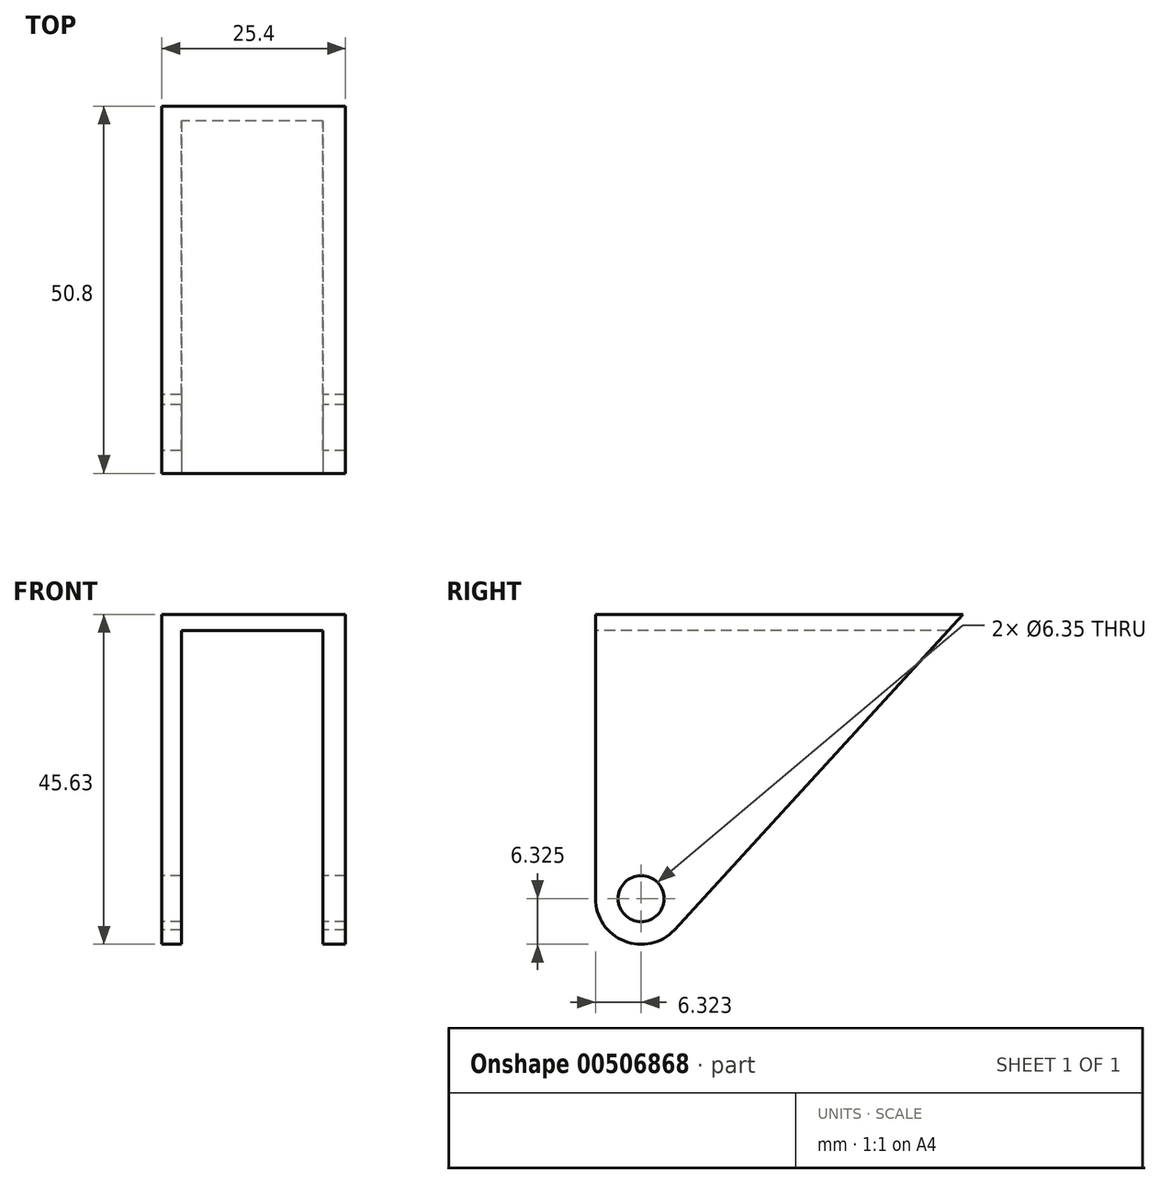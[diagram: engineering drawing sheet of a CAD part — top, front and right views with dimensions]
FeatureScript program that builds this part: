
annotation { "Feature Type Name" : "Feature", "Feature Type Description" : "" }
export const myFeature = defineFeature(function(context is Context, id is Id, definition is map)
    precondition{}
    {
        {
            var Q0;
            Q0=qCreatedBy(makeId("Right.planeOp"),FACE);
            var sketch = newSketch(context, id + "F0", { "sketchPlane" : qUnion([Q0])});
            skLineSegment(sketch, "E0", {"start": v(-6.1, -15.1) * mm, "end": v(-6.1, 24.2) * mm});
            skLineSegment(sketch, "E1", {"start": v(-6.1, 24.2) * mm, "end": v(44.7, 24.2) * mm});
            skLineSegment(sketch, "E2", {"start": v(44.7, 24.2) * mm, "end": v(4.82, -19.43) * mm});
            skArc(sketch, "E3", {"start": v(-6.1, -15.1) * mm, "mid": v(-2.11, -20.97) * mm, "end": v(4.82, -19.43) * mm});
            skSolve(sketch);
        }
        {
            var Q0;
            Q0=makeQuery(id+"FULionVZPmyyQfd_1.opExtrude","SWEPT_FACE",FACE,{"disambiguationData":[OSD([sQuery(id+"F0.wireOp",EDGE,"E2")])]});
            var Q1;
            Q1=makeQuery(id+"FULionVZPmyyQfd_1.opExtrude","SWEPT_FACE",FACE,{"disambiguationData":[OSD([sQuery(id+"F0.wireOp",EDGE,"E1")])]});
            var Q2;
            Q2=makeQuery(id+"F0.imprint","IMPRINT",FACE,{"disambiguationData":[TD([[makeQuery(id+"F0.imprint","IMPRINT",EDGE,{"derivedFrom":sQuery(id+"F0.wireOp",EDGE,"E0")}),-1.0]])]});
            var Q3;
            Q3=makeQuery(id+"FULionVZPmyyQfd_1.opExtrude","CAP_FACE",FACE,{"disambiguationData":[OSD([sQuery(id+"F0.wireOp",EDGE,"E0"),sQuery(id+"F0.wireOp",EDGE,"E1"),sQuery(id+"F0.wireOp",EDGE,"E2"),sQuery(id+"F0.wireOp",EDGE,"E3")])],"isStart":false});
            extrude(context, id + "F1", {"entities" : qUnion([Q0, Q1, Q2, Q3]), "depth" : 25.4 * mm});
        }
        {
            var Q0;
            Q0=sQuery(id+"F0.wireOp",VERTEX,"E3.center");
            var Q1;
            Q1=makeQuery(id+"F1.opExtrude","SWEPT_BODY",BODY,{"disambiguationData":[OSD([sQuery(id+"F0.wireOp",EDGE,"E0"),sQuery(id+"F0.wireOp",EDGE,"E1"),sQuery(id+"F0.wireOp",EDGE,"E2"),sQuery(id+"F0.wireOp",EDGE,"E3")])]});
            hole(context, id + "F2", {"style" : HoleStyle.SIMPLE, "endStyle" : HoleEndStyle.THROUGH, "oppositeDirection" : true, "holeDiameter" : 6.35 * mm, "isTappedThrough" : true, "tappedDepth" : 12.7 * mm, "tapClearance" : 3, "locations" : qUnion([Q0]), "scope" : qUnion([Q1])});
        }
        {
            var Q0;
            Q0=qCreatedBy(makeId("Front.planeOp"),FACE);
            var sketch = newSketch(context, id + "F3", { "sketchPlane" : qUnion([Q0])});
            skLineSegment(sketch, "E4.bottom", {"start": v(2.7, 21.96) * mm, "end": v(22.26, 21.96) * mm});
            skLineSegment(sketch, "E4.top", {"start": v(2.7, -33.69) * mm, "end": v(22.26, -33.69) * mm});
            skLineSegment(sketch, "E4.left", {"start": v(2.7, 21.96) * mm, "end": v(2.7, -33.69) * mm});
            skLineSegment(sketch, "E4.right", {"start": v(22.26, 21.96) * mm, "end": v(22.26, -33.69) * mm});
            skSolve(sketch);
        }
        {
            var Q0;
            Q0=makeQuery(id+"F3.imprint","IMPRINT",FACE,{"disambiguationData":[TD([[makeQuery(id+"F3.imprint","IMPRINT",EDGE,{"derivedFrom":sQuery(id+"F3.wireOp",EDGE,"E4.bottom")}),-1.0]])]});
            extrude(context, id + "F4", {"entities" : qUnion([Q0]), "operationType" : NewBodyOperationType.REMOVE, "depth" : -76.2 * mm, "offsetDistance" : 25.4 * mm});
        }
        {
            var Q0;
            Q0 = qSketchRegion(id + "F3", true);
            extrude(context, id + "F5", {"entities" : qUnion([Q0]), "operationType" : NewBodyOperationType.REMOVE, "depth" : 50.8 * mm, "offsetDistance" : 25.4 * mm});
        }
    });
